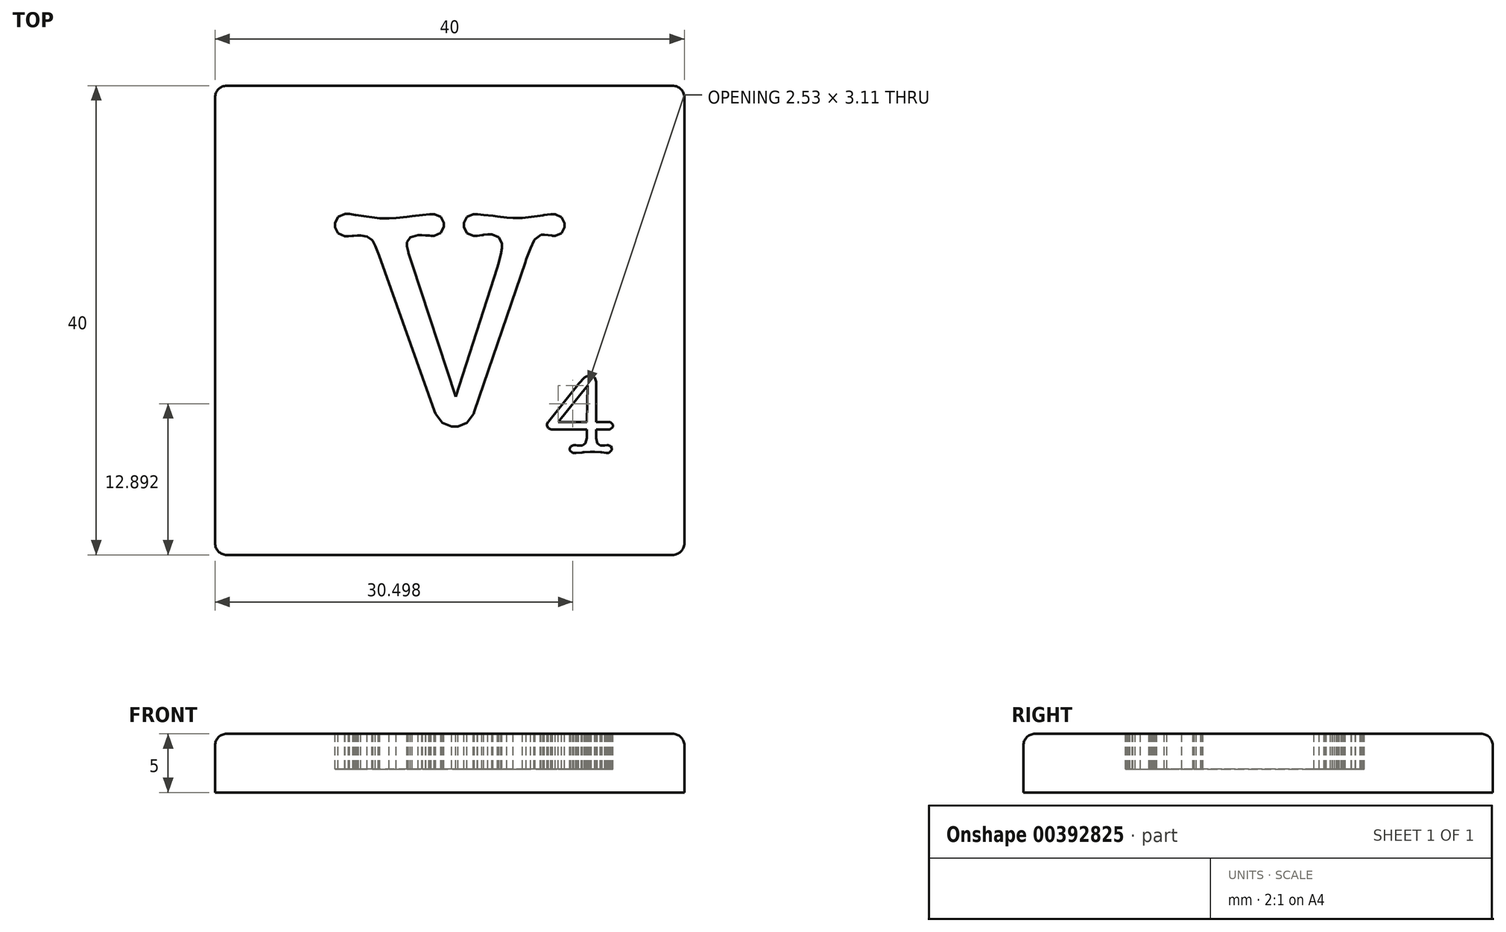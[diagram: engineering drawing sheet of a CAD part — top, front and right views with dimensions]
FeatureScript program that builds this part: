
annotation { "Feature Type Name" : "Feature", "Feature Type Description" : "" }
export const myFeature = defineFeature(function(context is Context, id is Id, definition is map)
    precondition{}
    {
        {
            var Q0;
            Q0=qCreatedBy(makeId("Top.planeOp"),FACE);
            var sketch = newSketch(context, id + "F0", { "sketchPlane" : qUnion([Q0])});
            skLineSegment(sketch, "E0.bottom", {"start": v(20, -20) * mm, "end": v(-20, -20) * mm});
            skLineSegment(sketch, "E0.top", {"start": v(20, 20) * mm, "end": v(-20, 20) * mm});
            skLineSegment(sketch, "E0.left", {"start": v(20, -20) * mm, "end": v(20, 20) * mm});
            skLineSegment(sketch, "E0.right", {"start": v(-20, -20) * mm, "end": v(-20, 20) * mm});
            skPoint(sketch, "E0.middle", {"position": v(0, 0) * mm});
            skSolve(sketch);
        }
        {
            var Q0;
            Q0=makeQuery(id+"F0.imprint","IMPRINT",FACE,{"disambiguationData":[TD([[makeQuery(id+"F0.imprint","IMPRINT",EDGE,{"derivedFrom":sQuery(id+"F0.wireOp",EDGE,"E0.bottom")}),-1.0]])]});
            extrude(context, id + "F1", {"entities" : qUnion([Q0]), "depth" : -5 * mm});
        }
        {
            var Q0;
            Q0=makeQuery(id+"F1.opExtrude","CAP_FACE",FACE,{"disambiguationData":[OSD([sQuery(id+"F0.wireOp",EDGE,"E0.bottom"),sQuery(id+"F0.wireOp",EDGE,"E0.top"),sQuery(id+"F0.wireOp",EDGE,"E0.left"),sQuery(id+"F0.wireOp",EDGE,"E0.right")])],"isStart":true});
            var Q1;
            Q1=makeQuery(id+"F1.opExtrude","SWEPT_EDGE",EDGE,{"disambiguationData":[OSD([sQuery(id+"F0.wireOp",EDGE,"E0.top"),sQuery(id+"F0.wireOp",EDGE,"E0.right")])]});
            var Q2;
            Q2=makeQuery(id+"F1.opExtrude","SWEPT_EDGE",EDGE,{"disambiguationData":[OSD([sQuery(id+"F0.wireOp",EDGE,"E0.top"),sQuery(id+"F0.wireOp",EDGE,"E0.left")])]});
            var Q3;
            Q3=makeQuery(id+"F1.opExtrude","SWEPT_EDGE",EDGE,{"disambiguationData":[OSD([sQuery(id+"F0.wireOp",EDGE,"E0.bottom"),sQuery(id+"F0.wireOp",EDGE,"E0.right")])]});
            var Q4;
            Q4=makeQuery(id+"F1.opExtrude","SWEPT_EDGE",EDGE,{"disambiguationData":[OSD([sQuery(id+"F0.wireOp",EDGE,"E0.bottom"),sQuery(id+"F0.wireOp",EDGE,"E0.left")])]});
            fillet(context, id + "F2", {"entities" : qUnion([Q0, Q1, Q2, Q3, Q4]), "radius" : 1 * mm, "tangentPropagation" : true, "allowEdgeOverflow" : false});
        }
        {
            var Q0;
            Q0=qCreatedBy(makeId("Top.planeOp"),FACE);
            var sketch = newSketch(context, id + "F3", { "sketchPlane" : qUnion([Q0])});
            skLineSegment(sketch, "E1", {"start": v(-3.21, 4.78) * mm, "end": v(0.52, -6.52) * mm});
            skLineSegment(sketch, "E2", {"start": v(0.52, -6.52) * mm, "end": v(4.06, 4.54) * mm});
            skLineSegment(sketch, "E3", {"start": v(4.06, 4.54) * mm, "end": v(4.13, 4.75) * mm});
            skLineSegment(sketch, "E4", {"start": v(4.13, 4.75) * mm, "end": v(4.36, 5.62) * mm});
            skLineSegment(sketch, "E5", {"start": v(4.36, 5.62) * mm, "end": v(4.46, 6.16) * mm});
            skLineSegment(sketch, "E6", {"start": v(4.46, 6.16) * mm, "end": v(4.46, 6.34) * mm});
            skLineSegment(sketch, "E7", {"start": v(4.46, 6.34) * mm, "end": v(4.46, 6.53) * mm});
            skLineSegment(sketch, "E8", {"start": v(4.46, 6.53) * mm, "end": v(4.2, 7.1) * mm});
            skLineSegment(sketch, "E9", {"start": v(4.2, 7.1) * mm, "end": v(3.6, 7.34) * mm});
            skLineSegment(sketch, "E10", {"start": v(3.6, 7.34) * mm, "end": v(3.4, 7.34) * mm});
            skLineSegment(sketch, "E11", {"start": v(3.4, 7.34) * mm, "end": v(3.25, 7.34) * mm});
            skLineSegment(sketch, "E12", {"start": v(3.25, 7.34) * mm, "end": v(2.88, 7.29) * mm});
            skLineSegment(sketch, "E13", {"start": v(2.88, 7.29) * mm, "end": v(2.82, 7.28) * mm});
            skLineSegment(sketch, "E14", {"start": v(2.82, 7.28) * mm, "end": v(2.75, 7.27) * mm});
            skLineSegment(sketch, "E15", {"start": v(2.75, 7.27) * mm, "end": v(2.36, 7.2) * mm});
            skLineSegment(sketch, "E16", {"start": v(2.36, 7.2) * mm, "end": v(2.24, 7.2) * mm});
            skLineSegment(sketch, "E17", {"start": v(2.24, 7.2) * mm, "end": v(2.04, 7.2) * mm});
            skLineSegment(sketch, "E18", {"start": v(2.04, 7.2) * mm, "end": v(1.46, 7.44) * mm});
            skLineSegment(sketch, "E19", {"start": v(1.46, 7.44) * mm, "end": v(1.2, 7.96) * mm});
            skLineSegment(sketch, "E20", {"start": v(1.2, 7.96) * mm, "end": v(1.2, 8.14) * mm});
            skLineSegment(sketch, "E21", {"start": v(1.2, 8.14) * mm, "end": v(1.2, 8.3) * mm});
            skLineSegment(sketch, "E22", {"start": v(1.2, 8.3) * mm, "end": v(1.45, 8.81) * mm});
            skLineSegment(sketch, "E23", {"start": v(1.45, 8.81) * mm, "end": v(2.02, 9.04) * mm});
            skLineSegment(sketch, "E24", {"start": v(2.02, 9.04) * mm, "end": v(2.2, 9.04) * mm});
            skLineSegment(sketch, "E25", {"start": v(2.2, 9.04) * mm, "end": v(2.38, 9.04) * mm});
            skLineSegment(sketch, "E26", {"start": v(2.38, 9.04) * mm, "end": v(2.9, 9) * mm});
            skLineSegment(sketch, "E27", {"start": v(2.9, 9) * mm, "end": v(3.7, 8.9) * mm});
            skLineSegment(sketch, "E28", {"start": v(3.7, 8.9) * mm, "end": v(3.89, 8.88) * mm});
            skLineSegment(sketch, "E29", {"start": v(3.89, 8.88) * mm, "end": v(4.08, 8.85) * mm});
            skLineSegment(sketch, "E30", {"start": v(4.08, 8.85) * mm, "end": v(4.88, 8.76) * mm});
            skLineSegment(sketch, "E31", {"start": v(4.88, 8.76) * mm, "end": v(5.42, 8.72) * mm});
            skLineSegment(sketch, "E32", {"start": v(5.42, 8.72) * mm, "end": v(5.6, 8.72) * mm});
            skLineSegment(sketch, "E33", {"start": v(5.6, 8.72) * mm, "end": v(6.18, 8.72) * mm});
            skLineSegment(sketch, "E34", {"start": v(6.18, 8.72) * mm, "end": v(7.72, 8.92) * mm});
            skLineSegment(sketch, "E35", {"start": v(7.72, 8.92) * mm, "end": v(7.95, 8.96) * mm});
            skLineSegment(sketch, "E36", {"start": v(7.95, 8.96) * mm, "end": v(8.02, 8.97) * mm});
            skLineSegment(sketch, "E37", {"start": v(8.02, 8.97) * mm, "end": v(8.6, 9.04) * mm});
            skLineSegment(sketch, "E38", {"start": v(8.6, 9.04) * mm, "end": v(8.8, 9.04) * mm});
            skLineSegment(sketch, "E39", {"start": v(8.8, 9.04) * mm, "end": v(8.98, 9.04) * mm});
            skLineSegment(sketch, "E40", {"start": v(8.98, 9.04) * mm, "end": v(9.53, 8.8) * mm});
            skLineSegment(sketch, "E41", {"start": v(9.53, 8.8) * mm, "end": v(9.78, 8.28) * mm});
            skLineSegment(sketch, "E42", {"start": v(9.78, 8.28) * mm, "end": v(9.78, 8.1) * mm});
            skLineSegment(sketch, "E43", {"start": v(9.78, 8.1) * mm, "end": v(9.78, 7.94) * mm});
            skLineSegment(sketch, "E44", {"start": v(9.78, 7.94) * mm, "end": v(9.53, 7.44) * mm});
            skLineSegment(sketch, "E45", {"start": v(9.53, 7.44) * mm, "end": v(8.98, 7.2) * mm});
            skLineSegment(sketch, "E46", {"start": v(8.98, 7.2) * mm, "end": v(8.8, 7.2) * mm});
            skLineSegment(sketch, "E47", {"start": v(8.8, 7.2) * mm, "end": v(8.77, 7.2) * mm});
            skLineSegment(sketch, "E48", {"start": v(8.77, 7.2) * mm, "end": v(8.7, 7.23) * mm});
            skLineSegment(sketch, "E49", {"start": v(8.7, 7.23) * mm, "end": v(8.7, 7.24) * mm});
            skLineSegment(sketch, "E50", {"start": v(8.7, 7.24) * mm, "end": v(8.08, 7.29) * mm});
            skLineSegment(sketch, "E51", {"start": v(8.08, 7.29) * mm, "end": v(7.95, 7.29) * mm});
            skLineSegment(sketch, "E52", {"start": v(7.95, 7.29) * mm, "end": v(7.77, 7.29) * mm});
            skLineSegment(sketch, "E53", {"start": v(7.77, 7.29) * mm, "end": v(7.27, 6.93) * mm});
            skLineSegment(sketch, "E54", {"start": v(7.27, 6.93) * mm, "end": v(7.22, 6.85) * mm});
            skLineSegment(sketch, "E55", {"start": v(7.22, 6.85) * mm, "end": v(7.18, 6.78) * mm});
            skLineSegment(sketch, "E56", {"start": v(7.18, 6.78) * mm, "end": v(6.89, 6.16) * mm});
            skLineSegment(sketch, "E57", {"start": v(6.89, 6.16) * mm, "end": v(6.53, 5.2) * mm});
            skLineSegment(sketch, "E58", {"start": v(6.53, 5.2) * mm, "end": v(6.44, 4.96) * mm});
            skLineSegment(sketch, "E59", {"start": v(6.44, 4.96) * mm, "end": v(2.1, -7.77) * mm});
            skLineSegment(sketch, "E60", {"start": v(2.1, -7.77) * mm, "end": v(2.03, -7.98) * mm});
            skLineSegment(sketch, "E61", {"start": v(2.03, -7.98) * mm, "end": v(1.46, -8.74) * mm});
            skLineSegment(sketch, "E62", {"start": v(1.46, -8.74) * mm, "end": v(0.7, -9.06) * mm});
            skLineSegment(sketch, "E63", {"start": v(0.7, -9.06) * mm, "end": v(0.44, -9.06) * mm});
            skLineSegment(sketch, "E64", {"start": v(0.44, -9.06) * mm, "end": v(0.17, -9.06) * mm});
            skLineSegment(sketch, "E65", {"start": v(0.17, -9.06) * mm, "end": v(-0.63, -8.74) * mm});
            skLineSegment(sketch, "E66", {"start": v(-0.63, -8.74) * mm, "end": v(-1.2, -7.98) * mm});
            skLineSegment(sketch, "E67", {"start": v(-1.2, -7.98) * mm, "end": v(-1.28, -7.77) * mm});
            skLineSegment(sketch, "E68", {"start": v(-1.28, -7.77) * mm, "end": v(-6.02, 5.54) * mm});
            skLineSegment(sketch, "E69", {"start": v(-6.02, 5.54) * mm, "end": v(-6.08, 5.7) * mm});
            skLineSegment(sketch, "E70", {"start": v(-6.08, 5.7) * mm, "end": v(-6.33, 6.34) * mm});
            skLineSegment(sketch, "E71", {"start": v(-6.33, 6.34) * mm, "end": v(-6.54, 6.74) * mm});
            skLineSegment(sketch, "E72", {"start": v(-6.54, 6.74) * mm, "end": v(-6.58, 6.79) * mm});
            skLineSegment(sketch, "E73", {"start": v(-6.58, 6.79) * mm, "end": v(-6.64, 6.86) * mm});
            skLineSegment(sketch, "E74", {"start": v(-6.64, 6.86) * mm, "end": v(-7.05, 7.13) * mm});
            skLineSegment(sketch, "E75", {"start": v(-7.05, 7.13) * mm, "end": v(-7.57, 7.24) * mm});
            skLineSegment(sketch, "E76", {"start": v(-7.57, 7.24) * mm, "end": v(-7.74, 7.24) * mm});
            skLineSegment(sketch, "E77", {"start": v(-7.74, 7.24) * mm, "end": v(-7.87, 7.24) * mm});
            skLineSegment(sketch, "E78", {"start": v(-7.87, 7.24) * mm, "end": v(-8.18, 7.22) * mm});
            skLineSegment(sketch, "E79", {"start": v(-8.18, 7.22) * mm, "end": v(-8.24, 7.2) * mm});
            skLineSegment(sketch, "E80", {"start": v(-8.24, 7.2) * mm, "end": v(-8.3, 7.2) * mm});
            skLineSegment(sketch, "E81", {"start": v(-8.3, 7.2) * mm, "end": v(-8.63, 7.18) * mm});
            skLineSegment(sketch, "E82", {"start": v(-8.63, 7.18) * mm, "end": v(-8.74, 7.18) * mm});
            skLineSegment(sketch, "E83", {"start": v(-8.74, 7.18) * mm, "end": v(-8.94, 7.18) * mm});
            skLineSegment(sketch, "E84", {"start": v(-8.94, 7.18) * mm, "end": v(-9.52, 7.42) * mm});
            skLineSegment(sketch, "E85", {"start": v(-9.52, 7.42) * mm, "end": v(-9.78, 7.94) * mm});
            skLineSegment(sketch, "E86", {"start": v(-9.78, 7.94) * mm, "end": v(-9.78, 8.1) * mm});
            skLineSegment(sketch, "E87", {"start": v(-9.78, 8.1) * mm, "end": v(-9.78, 8.29) * mm});
            skLineSegment(sketch, "E88", {"start": v(-9.78, 8.29) * mm, "end": v(-9.51, 8.83) * mm});
            skLineSegment(sketch, "E89", {"start": v(-9.51, 8.83) * mm, "end": v(-8.92, 9.06) * mm});
            skLineSegment(sketch, "E90", {"start": v(-8.92, 9.06) * mm, "end": v(-8.72, 9.06) * mm});
            skLineSegment(sketch, "E91", {"start": v(-8.72, 9.06) * mm, "end": v(-8.54, 9.06) * mm});
            skLineSegment(sketch, "E92", {"start": v(-8.54, 9.06) * mm, "end": v(-8.07, 9) * mm});
            skLineSegment(sketch, "E93", {"start": v(-8.07, 9) * mm, "end": v(-8, 8.98) * mm});
            skLineSegment(sketch, "E94", {"start": v(-8, 8.98) * mm, "end": v(-7.76, 8.94) * mm});
            skLineSegment(sketch, "E95", {"start": v(-7.76, 8.94) * mm, "end": v(-5.98, 8.7) * mm});
            skLineSegment(sketch, "E96", {"start": v(-5.98, 8.7) * mm, "end": v(-5.38, 8.7) * mm});
            skLineSegment(sketch, "E97", {"start": v(-5.38, 8.7) * mm, "end": v(-5.18, 8.7) * mm});
            skLineSegment(sketch, "E98", {"start": v(-5.18, 8.7) * mm, "end": v(-4.56, 8.74) * mm});
            skLineSegment(sketch, "E99", {"start": v(-4.56, 8.74) * mm, "end": v(-3.64, 8.84) * mm});
            skLineSegment(sketch, "E100", {"start": v(-3.64, 8.84) * mm, "end": v(-3.43, 8.86) * mm});
            skLineSegment(sketch, "E101", {"start": v(-3.43, 8.86) * mm, "end": v(-3.21, 8.9) * mm});
            skLineSegment(sketch, "E102", {"start": v(-3.21, 8.9) * mm, "end": v(-2.3, 9) * mm});
            skLineSegment(sketch, "E103", {"start": v(-2.3, 9) * mm, "end": v(-1.7, 9.04) * mm});
            skLineSegment(sketch, "E104", {"start": v(-1.7, 9.04) * mm, "end": v(-1.5, 9.04) * mm});
            skLineSegment(sketch, "E105", {"start": v(-1.5, 9.04) * mm, "end": v(-1.31, 9.04) * mm});
            skLineSegment(sketch, "E106", {"start": v(-1.31, 9.04) * mm, "end": v(-0.76, 8.82) * mm});
            skLineSegment(sketch, "E107", {"start": v(-0.76, 8.82) * mm, "end": v(-0.52, 8.33) * mm});
            skLineSegment(sketch, "E108", {"start": v(-0.52, 8.33) * mm, "end": v(-0.52, 8.16) * mm});
            skLineSegment(sketch, "E109", {"start": v(-0.52, 8.16) * mm, "end": v(-0.52, 7.99) * mm});
            skLineSegment(sketch, "E110", {"start": v(-0.52, 7.99) * mm, "end": v(-0.77, 7.45) * mm});
            skLineSegment(sketch, "E111", {"start": v(-0.77, 7.45) * mm, "end": v(-1.33, 7.2) * mm});
            skLineSegment(sketch, "E112", {"start": v(-1.33, 7.2) * mm, "end": v(-1.52, 7.2) * mm});
            skLineSegment(sketch, "E113", {"start": v(-1.52, 7.2) * mm, "end": v(-1.58, 7.2) * mm});
            skLineSegment(sketch, "E114", {"start": v(-1.58, 7.2) * mm, "end": v(-1.73, 7.23) * mm});
            skLineSegment(sketch, "E115", {"start": v(-1.73, 7.23) * mm, "end": v(-1.76, 7.24) * mm});
            skLineSegment(sketch, "E116", {"start": v(-1.76, 7.24) * mm, "end": v(-2.02, 7.24) * mm});
            skLineSegment(sketch, "E117", {"start": v(-2.02, 7.24) * mm, "end": v(-2.05, 7.24) * mm});
            skLineSegment(sketch, "E118", {"start": v(-2.05, 7.24) * mm, "end": v(-2.37, 7.26) * mm});
            skLineSegment(sketch, "E119", {"start": v(-2.37, 7.26) * mm, "end": v(-2.47, 7.26) * mm});
            skLineSegment(sketch, "E120", {"start": v(-2.47, 7.26) * mm, "end": v(-2.7, 7.26) * mm});
            skLineSegment(sketch, "E121", {"start": v(-2.7, 7.26) * mm, "end": v(-3.35, 7.08) * mm});
            skLineSegment(sketch, "E122", {"start": v(-3.35, 7.08) * mm, "end": v(-3.64, 6.66) * mm});
            skLineSegment(sketch, "E123", {"start": v(-3.64, 6.66) * mm, "end": v(-3.64, 6.52) * mm});
            skLineSegment(sketch, "E124", {"start": v(-3.64, 6.52) * mm, "end": v(-3.64, 6.32) * mm});
            skLineSegment(sketch, "E125", {"start": v(-3.64, 6.32) * mm, "end": v(-3.53, 5.8) * mm});
            skLineSegment(sketch, "E126", {"start": v(-3.53, 5.8) * mm, "end": v(-3.5, 5.73) * mm});
            skLineSegment(sketch, "E127", {"start": v(-3.5, 5.73) * mm, "end": v(-3.21, 4.78) * mm});
            skSolve(sketch);
        }
        {
            var Q0;
            Q0=qCreatedBy(makeId("Top.planeOp"),FACE);
            var sketch = newSketch(context, id + "F4", { "sketchPlane" : qUnion([Q0])});
            skLineSegment(sketch, "E128", {"start": v(12.48, -5.38) * mm, "end": v(12.48, -8.67) * mm});
            skLineSegment(sketch, "E129", {"start": v(12.48, -8.67) * mm, "end": v(13.6, -8.67) * mm});
            skLineSegment(sketch, "E130", {"start": v(13.6, -8.67) * mm, "end": v(13.68, -8.67) * mm});
            skLineSegment(sketch, "E131", {"start": v(13.68, -8.67) * mm, "end": v(13.92, -8.9) * mm});
            skLineSegment(sketch, "E132", {"start": v(13.92, -8.9) * mm, "end": v(13.92, -8.99) * mm});
            skLineSegment(sketch, "E133", {"start": v(13.92, -8.99) * mm, "end": v(13.92, -9.07) * mm});
            skLineSegment(sketch, "E134", {"start": v(13.92, -9.07) * mm, "end": v(13.67, -9.31) * mm});
            skLineSegment(sketch, "E135", {"start": v(13.67, -9.31) * mm, "end": v(13.58, -9.31) * mm});
            skLineSegment(sketch, "E136", {"start": v(13.58, -9.31) * mm, "end": v(12.48, -9.31) * mm});
            skLineSegment(sketch, "E137", {"start": v(12.48, -9.31) * mm, "end": v(12.48, -9.9) * mm});
            skLineSegment(sketch, "E138", {"start": v(12.48, -9.9) * mm, "end": v(12.48, -10.04) * mm});
            skLineSegment(sketch, "E139", {"start": v(12.48, -10.04) * mm, "end": v(12.58, -10.49) * mm});
            skLineSegment(sketch, "E140", {"start": v(12.58, -10.49) * mm, "end": v(12.83, -10.68) * mm});
            skLineSegment(sketch, "E141", {"start": v(12.83, -10.68) * mm, "end": v(12.9, -10.68) * mm});
            skLineSegment(sketch, "E142", {"start": v(12.9, -10.68) * mm, "end": v(12.99, -10.68) * mm});
            skLineSegment(sketch, "E143", {"start": v(12.99, -10.68) * mm, "end": v(13.19, -10.67) * mm});
            skLineSegment(sketch, "E144", {"start": v(13.19, -10.67) * mm, "end": v(13.22, -10.67) * mm});
            skLineSegment(sketch, "E145", {"start": v(13.22, -10.67) * mm, "end": v(13.42, -10.65) * mm});
            skLineSegment(sketch, "E146", {"start": v(13.42, -10.65) * mm, "end": v(13.5, -10.65) * mm});
            skLineSegment(sketch, "E147", {"start": v(13.5, -10.65) * mm, "end": v(13.72, -10.73) * mm});
            skLineSegment(sketch, "E148", {"start": v(13.72, -10.73) * mm, "end": v(13.82, -10.9) * mm});
            skLineSegment(sketch, "E149", {"start": v(13.82, -10.9) * mm, "end": v(13.82, -10.97) * mm});
            skLineSegment(sketch, "E150", {"start": v(13.82, -10.97) * mm, "end": v(13.82, -11.05) * mm});
            skLineSegment(sketch, "E151", {"start": v(13.82, -11.05) * mm, "end": v(13.56, -11.3) * mm});
            skLineSegment(sketch, "E152", {"start": v(13.56, -11.3) * mm, "end": v(13.48, -11.3) * mm});
            skLineSegment(sketch, "E153", {"start": v(13.48, -11.3) * mm, "end": v(13.34, -11.3) * mm});
            skLineSegment(sketch, "E154", {"start": v(13.34, -11.3) * mm, "end": v(12.97, -11.26) * mm});
            skLineSegment(sketch, "E155", {"start": v(12.97, -11.26) * mm, "end": v(12.92, -11.25) * mm});
            skLineSegment(sketch, "E156", {"start": v(12.92, -11.25) * mm, "end": v(12.87, -11.24) * mm});
            skLineSegment(sketch, "E157", {"start": v(12.87, -11.24) * mm, "end": v(12.35, -11.2) * mm});
            skLineSegment(sketch, "E158", {"start": v(12.35, -11.2) * mm, "end": v(12.18, -11.2) * mm});
            skLineSegment(sketch, "E159", {"start": v(12.18, -11.2) * mm, "end": v(11.98, -11.2) * mm});
            skLineSegment(sketch, "E160", {"start": v(11.98, -11.2) * mm, "end": v(11.47, -11.25) * mm});
            skLineSegment(sketch, "E161", {"start": v(11.47, -11.25) * mm, "end": v(11.38, -11.26) * mm});
            skLineSegment(sketch, "E162", {"start": v(11.38, -11.26) * mm, "end": v(11.3, -11.27) * mm});
            skLineSegment(sketch, "E163", {"start": v(11.3, -11.27) * mm, "end": v(10.76, -11.31) * mm});
            skLineSegment(sketch, "E164", {"start": v(10.76, -11.31) * mm, "end": v(10.58, -11.31) * mm});
            skLineSegment(sketch, "E165", {"start": v(10.58, -11.31) * mm, "end": v(10.5, -11.31) * mm});
            skLineSegment(sketch, "E166", {"start": v(10.5, -11.31) * mm, "end": v(10.22, -11.07) * mm});
            skLineSegment(sketch, "E167", {"start": v(10.22, -11.07) * mm, "end": v(10.22, -11) * mm});
            skLineSegment(sketch, "E168", {"start": v(10.22, -11) * mm, "end": v(10.22, -10.93) * mm});
            skLineSegment(sketch, "E169", {"start": v(10.22, -10.93) * mm, "end": v(10.33, -10.73) * mm});
            skLineSegment(sketch, "E170", {"start": v(10.33, -10.73) * mm, "end": v(10.58, -10.65) * mm});
            skLineSegment(sketch, "E171", {"start": v(10.58, -10.65) * mm, "end": v(10.66, -10.65) * mm});
            skLineSegment(sketch, "E172", {"start": v(10.66, -10.65) * mm, "end": v(10.73, -10.65) * mm});
            skLineSegment(sketch, "E173", {"start": v(10.73, -10.65) * mm, "end": v(10.9, -10.66) * mm});
            skLineSegment(sketch, "E174", {"start": v(10.9, -10.66) * mm, "end": v(10.94, -10.67) * mm});
            skLineSegment(sketch, "E175", {"start": v(10.94, -10.67) * mm, "end": v(10.97, -10.67) * mm});
            skLineSegment(sketch, "E176", {"start": v(10.97, -10.67) * mm, "end": v(11.22, -10.68) * mm});
            skLineSegment(sketch, "E177", {"start": v(11.22, -10.68) * mm, "end": v(11.31, -10.68) * mm});
            skLineSegment(sketch, "E178", {"start": v(11.31, -10.68) * mm, "end": v(11.58, -10.49) * mm});
            skLineSegment(sketch, "E179", {"start": v(11.58, -10.49) * mm, "end": v(11.7, -10.04) * mm});
            skLineSegment(sketch, "E180", {"start": v(11.7, -10.04) * mm, "end": v(11.7, -9.9) * mm});
            skLineSegment(sketch, "E181", {"start": v(11.7, -9.9) * mm, "end": v(11.7, -9.31) * mm});
            skLineSegment(sketch, "E182", {"start": v(11.7, -9.31) * mm, "end": v(8.75, -9.31) * mm});
            skLineSegment(sketch, "E183", {"start": v(8.75, -9.31) * mm, "end": v(8.66, -9.31) * mm});
            skLineSegment(sketch, "E184", {"start": v(8.66, -9.31) * mm, "end": v(8.42, -9.22) * mm});
            skLineSegment(sketch, "E185", {"start": v(8.42, -9.22) * mm, "end": v(8.3, -9) * mm});
            skLineSegment(sketch, "E186", {"start": v(8.3, -9) * mm, "end": v(8.3, -8.93) * mm});
            skLineSegment(sketch, "E187", {"start": v(8.3, -8.93) * mm, "end": v(8.3, -8.86) * mm});
            skLineSegment(sketch, "E188", {"start": v(8.3, -8.86) * mm, "end": v(8.4, -8.65) * mm});
            skLineSegment(sketch, "E189", {"start": v(8.4, -8.65) * mm, "end": v(8.41, -8.63) * mm});
            skLineSegment(sketch, "E190", {"start": v(8.41, -8.63) * mm, "end": v(10.94, -5.5) * mm});
            skLineSegment(sketch, "E191", {"start": v(10.94, -5.5) * mm, "end": v(11, -5.41) * mm});
            skLineSegment(sketch, "E192", {"start": v(11, -5.41) * mm, "end": v(11.5, -4.87) * mm});
            skLineSegment(sketch, "E193", {"start": v(11.5, -4.87) * mm, "end": v(11.53, -4.85) * mm});
            skLineSegment(sketch, "E194", {"start": v(11.53, -4.85) * mm, "end": v(11.56, -4.83) * mm});
            skLineSegment(sketch, "E195", {"start": v(11.56, -4.83) * mm, "end": v(11.86, -4.7) * mm});
            skLineSegment(sketch, "E196", {"start": v(11.86, -4.7) * mm, "end": v(11.96, -4.7) * mm});
            skLineSegment(sketch, "E197", {"start": v(11.96, -4.7) * mm, "end": v(12.06, -4.7) * mm});
            skLineSegment(sketch, "E198", {"start": v(12.06, -4.7) * mm, "end": v(12.35, -4.87) * mm});
            skLineSegment(sketch, "E199", {"start": v(12.35, -4.87) * mm, "end": v(12.48, -5.25) * mm});
            skLineSegment(sketch, "E200", {"start": v(12.48, -5.25) * mm, "end": v(12.48, -5.38) * mm});
            skLineSegment(sketch, "E201", {"start": v(9.23, -8.67) * mm, "end": v(11.7, -8.67) * mm});
            skLineSegment(sketch, "E202", {"start": v(11.7, -8.67) * mm, "end": v(11.76, -5.55) * mm});
            skLineSegment(sketch, "E203", {"start": v(11.76, -5.55) * mm, "end": v(9.23, -8.67) * mm});
            skSolve(sketch);
        }
        {
            var Q0;
            Q0=qSketchRegion(id+"F3",true);
            var Q1;
            Q1=qSketchRegion(id+"F4",true);
            extrude(context, id + "F5", {"entities" : qUnion([Q0, Q1]), "depth" : -3 * mm});
        }
    });
